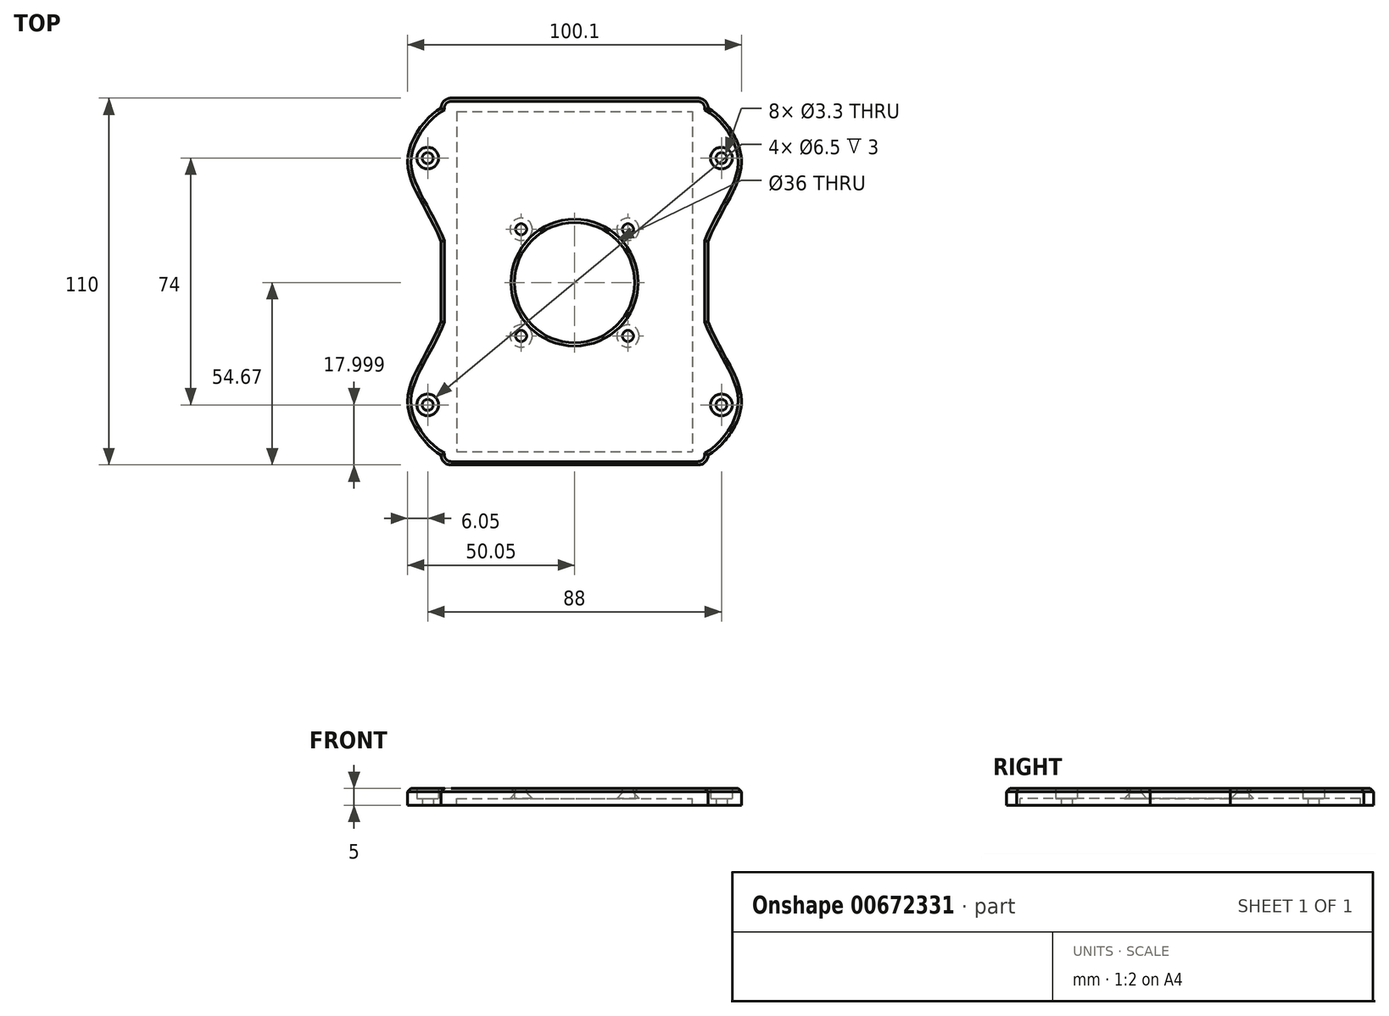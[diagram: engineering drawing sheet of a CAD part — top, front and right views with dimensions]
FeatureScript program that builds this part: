
annotation { "Feature Type Name" : "Feature", "Feature Type Description" : "" }
export const myFeature = defineFeature(function(context is Context, id is Id, definition is map)
    precondition{}
    {
        {
            var Q0;
            Q0=qCreatedBy(makeId("Top.planeOp"),FACE);
            var sketch = newSketch(context, id + "F0", { "sketchPlane" : qUnion([Q0])});
            skLineSegment(sketch, "E0.bottom", {"start": v(-37, 55.33) * mm, "end": v(37, 55.33) * mm});
            skLineSegment(sketch, "E0.top", {"start": v(-37, -54.67) * mm, "end": v(37, -54.67) * mm});
            skLineSegment(sketch, "E0.left", {"start": v(-40, 52.33) * mm, "end": v(-40, -51.67) * mm});
            skLineSegment(sketch, "E0.right", {"start": v(40, 52.33) * mm, "end": v(40, -51.67) * mm});
            skPoint(sketch, "E1.visualSharp", {"position": v(-40, 55.33) * mm});
            skArc(sketch, "E1.filletArc", {"start": v(-37, 55.33) * mm, "mid": v(-39.12, 54.45) * mm, "end": v(-40, 52.33) * mm});
            skPoint(sketch, "E2.visualSharp", {"position": v(40, 55.33) * mm});
            skArc(sketch, "E2.filletArc", {"start": v(40, 52.33) * mm, "mid": v(39.12, 54.45) * mm, "end": v(37, 55.33) * mm});
            skPoint(sketch, "E3.visualSharp", {"position": v(-40, -54.67) * mm});
            skArc(sketch, "E3.filletArc", {"start": v(-40, -51.67) * mm, "mid": v(-39.12, -53.8) * mm, "end": v(-37, -54.67) * mm});
            skPoint(sketch, "E4.visualSharp", {"position": v(40, -54.67) * mm});
            skArc(sketch, "E4.filletArc", {"start": v(37, -54.67) * mm, "mid": v(39.12, -53.8) * mm, "end": v(40, -51.67) * mm});
            skLineSegment(sketch, "E5.bottom", {"start": v(-35.25, 51.33) * mm, "end": v(35.25, 51.33) * mm});
            skLineSegment(sketch, "E5.top", {"start": v(-35.25, -50.67) * mm, "end": v(35.25, -50.67) * mm});
            skLineSegment(sketch, "E5.left", {"start": v(-35.25, 51.33) * mm, "end": v(-35.25, -50.67) * mm});
            skLineSegment(sketch, "E5.right", {"start": v(35.25, 51.33) * mm, "end": v(35.25, -50.67) * mm});
            skPoint(sketch, "E6", {"position": v(-30.86, 36.33) * mm});
            skPoint(sketch, "E7.MirrorP", {"position": v(30.86, 36.33) * mm});
            skPoint(sketch, "E8", {"position": v(-30.86, -40.27) * mm});
            skPoint(sketch, "E9.MirrorP", {"position": v(30.86, -40.27) * mm});
            skFitSpline(sketch, "E10", {"points": [v(40, 52.33) * mm, v(50, 37.33) * mm, v(40, 12.33) * mm], "startDerivative": vector(28.09, -14.91) * mm, "endDerivative": vector(-23.57, -58.35) * mm});
            skFitSpline(sketch, "E11.MirrorCS", {"points": [v(-40, 52.33) * mm, v(-50, 37.33) * mm, v(-40, 12.33) * mm], "startDerivative": vector(-28.09, -14.91) * mm, "endDerivative": vector(23.57, -58.35) * mm});
            skFitSpline(sketch, "E12.MirrorCS", {"points": [v(-40, -51.67) * mm, v(-50, -36.67) * mm, v(-40, -11.67) * mm], "startDerivative": vector(-28.09, 14.91) * mm, "endDerivative": vector(23.57, 58.35) * mm});
            skFitSpline(sketch, "E13.MirrorCS", {"points": [v(40, -51.67) * mm, v(50, -36.67) * mm, v(40, -11.67) * mm], "startDerivative": vector(28.09, 14.91) * mm, "endDerivative": vector(-23.57, 58.35) * mm});
            skPoint(sketch, "E14", {"position": v(-44, 37.33) * mm});
            skPoint(sketch, "E15.MirrorP", {"position": v(44, 37.33) * mm});
            skPoint(sketch, "E16.MirrorP", {"position": v(-44, -36.67) * mm});
            skPoint(sketch, "E17.MirrorP", {"position": v(44, -36.67) * mm});
            skSolve(sketch);
        }
        {
            var Q0;
            Q0 = qSketchRegion(id + "F0", true);
            extrude(context, id + "F1", {"entities" : qUnion([Q0]), "oppositeDirection" : true, "depth" : 5 * mm, "offsetDistance" : 25 * mm});
        }
        {
            var Q0;
            Q0=sQuery(id+"F0.wireOp",VERTEX,"E14");
            var Q1;
            Q1=sQuery(id+"F0.wireOp",VERTEX,"E15.MirrorP");
            var Q2;
            Q2=sQuery(id+"F0.wireOp",VERTEX,"E17.MirrorP");
            var Q3;
            Q3=sQuery(id+"F0.wireOp",VERTEX,"E16.MirrorP");
            var Q4;
            Q4=makeQuery(id+"F1.opExtrude","SWEPT_BODY",BODY,{"disambiguationData":[OSD([sQuery(id+"F0.wireOp",EDGE,"E0.bottom"),sQuery(id+"F0.wireOp",EDGE,"E0.top"),sQuery(id+"F0.wireOp",EDGE,"E0.left"),sQuery(id+"F0.wireOp",EDGE,"E0.right"),sQuery(id+"F0.wireOp",EDGE,"E1.filletArc"),sQuery(id+"F0.wireOp",EDGE,"E2.filletArc"),sQuery(id+"F0.wireOp",EDGE,"E3.filletArc"),sQuery(id+"F0.wireOp",EDGE,"E4.filletArc"),sQuery(id+"F0.wireOp",EDGE,"E10"),sQuery(id+"F0.wireOp",EDGE,"E11.MirrorCS"),sQuery(id+"F0.wireOp",EDGE,"E12.MirrorCS"),sQuery(id+"F0.wireOp",EDGE,"E13.MirrorCS")])]});
            hole(context, id + "F2", {"style" : HoleStyle.C_BORE, "endStyle" : HoleEndStyle.THROUGH, "standardTappedOrClearance" : lookupTablePath({ "standard" : "ISO", "fit" : "Normal", "size" : "M3", "type" : "Clearance" }), "standardBlindInLast" : lookupTablePath({ "fit" : "Standard", "standard" : "ISO", "size" : "M3", "type" : "Clearance" }), "holeDiameter" : 3.3 * mm, "cBoreDiameter" : 6.5 * mm, "cBoreDepth" : 3 * mm, "majorDiameter" : 5 * mm, "isTappedThrough" : true, "tappedDepth" : 12 * mm, "tapClearance" : 3, "startFromSketch" : true, "locations" : qUnion([Q0, Q1, Q2, Q3]), "scope" : qUnion([Q4])});
        }
        {
            var Q0;
            Q0=makeQuery(id+"F0.imprint","IMPRINT",FACE,{"disambiguationData":[TD([[makeQuery(id+"F0.imprint","IMPRINT",EDGE,{"derivedFrom":sQuery(id+"F0.wireOp",EDGE,"E5.bottom")}),-1.0]])]});
            extrude(context, id + "F3", {"entities" : qUnion([Q0]), "operationType" : NewBodyOperationType.ADD, "oppositeDirection" : true, "depth" : 3 * mm, "offsetDistance" : 25 * mm});
        }
        {
            var Q0;
            Q0=makeQuery(id+"F3.opExtrude","CAP_FACE",FACE,{"disambiguationData":[OSD([sQuery(id+"F0.wireOp",EDGE,"E5.bottom"),sQuery(id+"F0.wireOp",EDGE,"E5.top"),sQuery(id+"F0.wireOp",EDGE,"E5.left"),sQuery(id+"F0.wireOp",EDGE,"E5.right")])],"isStart":false});
            var sketch = newSketch(context, id + "F4", { "sketchPlane" : qUnion([Q0])});
            skCircle(sketch, "E18", {"center": v(0, 0) * mm, "radius": 18 * mm});
            skPoint(sketch, "E19", {"position": v(-16, -16) * mm});
            skPoint(sketch, "E20.MirrorP", {"position": v(-16, 16) * mm});
            skPoint(sketch, "E21.MirrorP", {"position": v(16, -16) * mm});
            skPoint(sketch, "E22.MirrorP", {"position": v(16, 16) * mm});
            skSolve(sketch);
        }
        {
            var Q0;
            Q0=sQuery(id+"F4.wireOp",VERTEX,"E19");
            var Q1;
            Q1=sQuery(id+"F4.wireOp",VERTEX,"E20.MirrorP");
            var Q2;
            Q2=sQuery(id+"F4.wireOp",VERTEX,"E22.MirrorP");
            var Q3;
            Q3=sQuery(id+"F4.wireOp",VERTEX,"E21.MirrorP");
            var Q4;
            Q4=makeQuery(id+"F1.opExtrude","SWEPT_BODY",BODY,{"disambiguationData":[OSD([sQuery(id+"F0.wireOp",EDGE,"E0.bottom"),sQuery(id+"F0.wireOp",EDGE,"E0.top"),sQuery(id+"F0.wireOp",EDGE,"E0.left"),sQuery(id+"F0.wireOp",EDGE,"E0.right"),sQuery(id+"F0.wireOp",EDGE,"E1.filletArc"),sQuery(id+"F0.wireOp",EDGE,"E2.filletArc"),sQuery(id+"F0.wireOp",EDGE,"E3.filletArc"),sQuery(id+"F0.wireOp",EDGE,"E4.filletArc"),sQuery(id+"F0.wireOp",EDGE,"E5.bottom"),sQuery(id+"F0.wireOp",EDGE,"E5.top"),sQuery(id+"F0.wireOp",EDGE,"E5.left"),sQuery(id+"F0.wireOp",EDGE,"E5.right"),sQuery(id+"F0.wireOp",EDGE,"E10"),sQuery(id+"F0.wireOp",EDGE,"E11.MirrorCS"),sQuery(id+"F0.wireOp",EDGE,"E12.MirrorCS"),sQuery(id+"F0.wireOp",EDGE,"E13.MirrorCS")])]});
            hole(context, id + "F5", {"style" : HoleStyle.C_SINK, "endStyle" : HoleEndStyle.THROUGH, "holeDiameter" : 3.3 * mm, "cSinkDiameter" : 6.72 * mm, "cSinkAngle" : 90 * degree, "majorDiameter" : 5 * mm, "isTappedThrough" : true, "tappedDepth" : 12 * mm, "tapClearance" : 3, "startFromSketch" : true, "locations" : qUnion([Q0, Q1, Q2, Q3]), "scope" : qUnion([Q4])});
        }
        {
            var Q0;
            Q0 = qSketchRegion(id + "F4", true);
            extrude(context, id + "F6", {"entities" : qUnion([Q0]), "operationType" : NewBodyOperationType.REMOVE, "oppositeDirection" : true, "depth" : 25 * mm, "offsetDistance" : 25 * mm});
        }
        {
            var Q0;
            Q0=makeQuery(id+"F1.opExtrude","CAP_EDGE",EDGE,{"disambiguationData":[OSD([sQuery(id+"F0.wireOp",EDGE,"E0.bottom")])],"isStart":true});
            var Q1;
            Q1=makeQuery(id+"F1.opExtrude","CAP_EDGE",EDGE,{"disambiguationData":[OSD([sQuery(id+"F0.wireOp",EDGE,"E11.MirrorCS")])],"isStart":true});
            var Q2;
            Q2=makeQuery(id+"F1.opExtrude","CAP_EDGE",EDGE,{"disambiguationData":[OSD([sQuery(id+"F0.wireOp",EDGE,"E0.left")])],"isStart":true});
            var Q3;
            Q3=makeQuery(id+"F1.opExtrude","CAP_EDGE",EDGE,{"disambiguationData":[OSD([sQuery(id+"F0.wireOp",EDGE,"E12.MirrorCS")])],"isStart":true});
            var Q4;
            Q4=makeQuery(id+"F1.opExtrude","CAP_EDGE",EDGE,{"disambiguationData":[OSD([sQuery(id+"F0.wireOp",EDGE,"E3.filletArc")])],"isStart":true});
            var Q5;
            Q5=makeQuery(id+"F1.opExtrude","CAP_EDGE",EDGE,{"disambiguationData":[OSD([sQuery(id+"F0.wireOp",EDGE,"E13.MirrorCS")])],"isStart":true});
            var Q6;
            Q6=makeQuery(id+"F1.opExtrude","CAP_EDGE",EDGE,{"disambiguationData":[OSD([sQuery(id+"F0.wireOp",EDGE,"E0.top")])],"isStart":true});
            var Q7;
            Q7=makeQuery(id+"F1.opExtrude","CAP_EDGE",EDGE,{"disambiguationData":[OSD([sQuery(id+"F0.wireOp",EDGE,"E4.filletArc")])],"isStart":true});
            var Q8;
            Q8=makeQuery(id+"F1.opExtrude","CAP_EDGE",EDGE,{"disambiguationData":[OSD([sQuery(id+"F0.wireOp",EDGE,"E0.right")])],"isStart":true});
            var Q9;
            Q9=makeQuery(id+"F1.opExtrude","CAP_EDGE",EDGE,{"disambiguationData":[OSD([sQuery(id+"F0.wireOp",EDGE,"E10")])],"isStart":true});
            var Q10;
            Q10=makeQuery(id+"F1.opExtrude","CAP_EDGE",EDGE,{"disambiguationData":[OSD([sQuery(id+"F0.wireOp",EDGE,"E2.filletArc")])],"isStart":true});
            var Q11;
            Q11=makeQuery(id+"F1.opExtrude","CAP_EDGE",EDGE,{"disambiguationData":[OSD([sQuery(id+"F0.wireOp",EDGE,"E1.filletArc")])],"isStart":true});
            var Q12;
            {var subQ0=sQuery(id+"F0.wireOp",EDGE,"E5.right");var subQ1=sQuery(id+"F0.wireOp",EDGE,"E5.left");var subQ2=sQuery(id+"F0.wireOp",EDGE,"E5.top");var subQ3=sQuery(id+"F0.wireOp",EDGE,"E5.bottom");Q12=makeQuery(id+"F6.boolean.opBoolean","INTERSECT",EDGE,{"derivedFrom":[makeQuery(id+"F3.boolean.opBoolean","MERGE",FACE,{"derivedFrom":[makeQuery(id+"F1.opExtrude","CAP_FACE",FACE,{"disambiguationData":[OSD([sQuery(id+"F0.wireOp",EDGE,"E0.bottom"),sQuery(id+"F0.wireOp",EDGE,"E0.top"),sQuery(id+"F0.wireOp",EDGE,"E0.left"),sQuery(id+"F0.wireOp",EDGE,"E0.right"),sQuery(id+"F0.wireOp",EDGE,"E1.filletArc"),sQuery(id+"F0.wireOp",EDGE,"E2.filletArc"),sQuery(id+"F0.wireOp",EDGE,"E3.filletArc"),sQuery(id+"F0.wireOp",EDGE,"E4.filletArc"),subQ3,subQ2,subQ1,subQ0,sQuery(id+"F0.wireOp",EDGE,"E10"),sQuery(id+"F0.wireOp",EDGE,"E11.MirrorCS"),sQuery(id+"F0.wireOp",EDGE,"E12.MirrorCS"),sQuery(id+"F0.wireOp",EDGE,"E13.MirrorCS")])],"isStart":true}),makeQuery(id+"F3.opExtrude","CAP_FACE",FACE,{"disambiguationData":[OSD([subQ3,subQ2,subQ1,subQ0])],"isStart":true})]}),makeQuery(id+"F6.opExtrude","SWEPT_FACE",FACE,{"disambiguationData":[OSD([sQuery(id+"F4.wireOp",EDGE,"E18")])]})]});}
            chamfer(context, id + "F7", {"entities" : qUnion([Q0, Q1, Q2, Q3, Q4, Q5, Q6, Q7, Q8, Q9, Q10, Q11, Q12]), "width" : 1 * mm, "tangentPropagation" : true});
        }
    });
